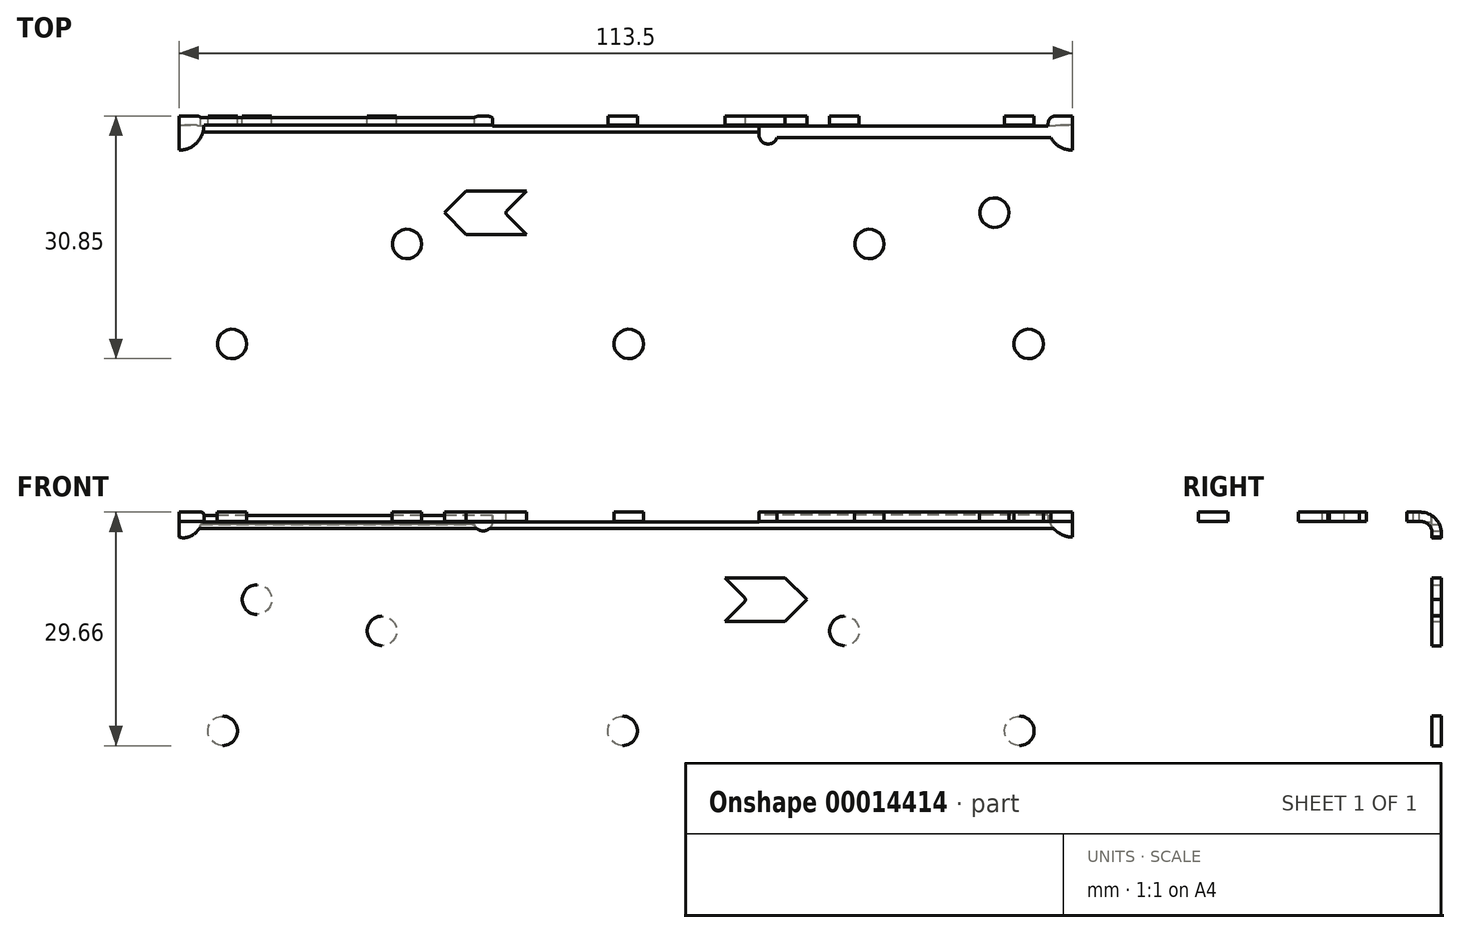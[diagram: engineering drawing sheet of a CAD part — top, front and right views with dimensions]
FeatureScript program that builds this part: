
annotation { "Feature Type Name" : "Feature", "Feature Type Description" : "" }
export const myFeature = defineFeature(function(context is Context, id is Id, definition is map)
    precondition{}
    {
        {
            var Q0;
            Q0=qCreatedBy(makeId("Top.planeOp"),FACE);
            var sketch = newSketch(context, id + "F0", { "sketchPlane" : qUnion([Q0])});
            skLineSegment(sketch, "E0", {"start": v(-34.93, 1.2) * mm, "end": v(-2.51, 1.2) * mm});
            skLineSegment(sketch, "E1", {"start": v(-34.93, 0) * mm, "end": v(-2.64, 0) * mm});
            skLineSegment(sketch, "E2", {"start": v(-1.2, 36.12) * mm, "end": v(-1.2, 2.51) * mm});
            skLineSegment(sketch, "E3", {"start": v(0, 36.12) * mm, "end": v(0, 2.64) * mm});
            skLineSegment(sketch, "E4", {"start": v(-1.2, 36.12) * mm, "end": v(0, 36.12) * mm});
            skLineSegment(sketch, "E5", {"start": v(-34.93, 1.2) * mm, "end": v(-34.93, 0) * mm});
            skLineSegment(sketch, "E6", {"start": v(-14.68, 8.33) * mm, "end": v(-14.68, 1.2) * mm});
            skLineSegment(sketch, "E7", {"start": v(-9.13, 8.33) * mm, "end": v(-9.13, 1.2) * mm});
            skLineSegment(sketch, "E8", {"start": v(-14.68, 8.33) * mm, "end": v(-9.13, 8.33) * mm});
            skArc(sketch, "E9", {"start": v(-2.51, 1.2) * mm, "mid": v(-1.58, 1.58) * mm, "end": v(-1.2, 2.51) * mm});
            skArc(sketch, "E10", {"start": v(-2.64, 0) * mm, "mid": v(-0.77, 0.77) * mm, "end": v(0, 2.64) * mm});
            skSolve(sketch);
        }
        {
            var Q0;
            Q0=makeQuery(id+"F0.imprint","IMPRINT",FACE,{"disambiguationData":[TD([[makeQuery(id+"F0.imprint","IMPRINT",EDGE,{"derivedFrom":sQuery(id+"F0.wireOp",EDGE,"E1")}),1.0]])]});
            extrude(context, id + "F1", {"entities" : qUnion([Q0]), "depth" : 113.5 * mm});
        }
        {
            var Q0;
            Q0=qCreatedBy(makeId("Front.planeOp"),FACE);
            var sketch = newSketch(context, id + "F2", { "sketchPlane" : qUnion([Q0])});
            skLineSegment(sketch, "E11", {"start": v(16.9, 1) * mm, "end": v(16.9, 3.38) * mm});
            skLineSegment(sketch, "E12", {"start": v(19.3, 3.38) * mm, "end": v(19.3, 1) * mm});
            skArc(sketch, "E13", {"start": v(16.9, 1) * mm, "mid": v(18.1, -0.19) * mm, "end": v(19.3, 1) * mm});
            skArc(sketch, "E14", {"start": v(19.3, 3.38) * mm, "mid": v(18.1, 4.57) * mm, "end": v(16.9, 3.38) * mm});
            skLineSegment(sketch, "E15", {"start": v(-47.23, -18.06) * mm, "end": v(-47.23, -18.06) * mm});
            skLineSegment(sketch, "E16", {"start": v(33.73, -5.36) * mm, "end": v(33.73, -5.36) * mm});
            skCircle(sketch, "E17", {"center": v(-50, -10.91) * mm, "radius": 1.88 * mm});
            skCircle(sketch, "E18", {"center": v(0.4, -10.91) * mm, "radius": 1.88 * mm});
            skCircle(sketch, "E19", {"center": v(51.2, -10.91) * mm, "radius": 1.88 * mm});
            skCircle(sketch, "E20", {"center": v(-27.78, 1.79) * mm, "radius": 1.88 * mm});
            skCircle(sketch, "E21", {"center": v(30.96, 1.79) * mm, "radius": 1.88 * mm});
            skCircle(sketch, "E22", {"center": v(46.83, 5.75) * mm, "radius": 1.88 * mm});
            skLineSegment(sketch, "E23", {"start": v(16.9, 15.68) * mm, "end": v(16.9, 16.87) * mm});
            skArc(sketch, "E24", {"start": v(16.9, 15.68) * mm, "mid": v(17.9, 14.5) * mm, "end": v(19.23, 15.28) * mm});
            skLineSegment(sketch, "E25", {"start": v(-56.75, 18.06) * mm, "end": v(-56.75, 16.87) * mm});
            skLineSegment(sketch, "E26", {"start": v(56.75, 16.87) * mm, "end": v(56.75, 18.06) * mm});
            skLineSegment(sketch, "E27", {"start": v(-20.25, 2.98) * mm, "end": v(2.38, 2.98) * mm});
            skLineSegment(sketch, "E28", {"start": v(-20.25, 8.53) * mm, "end": v(2.38, 8.53) * mm});
            skArc(sketch, "E29", {"start": v(-15.08, 6.03) * mm, "mid": v(-15.2, 5.75) * mm, "end": v(-15.08, 5.47) * mm});
            skLineSegment(sketch, "E30", {"start": v(-15.08, 5.47) * mm, "end": v(-12.6, 2.98) * mm});
            skLineSegment(sketch, "E31", {"start": v(-15.08, 6.03) * mm, "end": v(-12.58, 8.53) * mm});
            skLineSegment(sketch, "E32", {"start": v(-23.02, 5.75) * mm, "end": v(-20.25, 2.98) * mm});
            skLineSegment(sketch, "E33", {"start": v(-23.02, 5.75) * mm, "end": v(-20.25, 8.53) * mm});
            skLineSegment(sketch, "E34", {"start": v(-56.75, 16.87) * mm, "end": v(56.75, 16.87) * mm});
            skLineSegment(sketch, "E35", {"start": v(-56.75, 18.06) * mm, "end": v(56.75, 18.06) * mm});
            skArc(sketch, "E36", {"start": v(-56.75, 13.7) * mm, "mid": v(-54.52, 14.63) * mm, "end": v(-53.6, 16.87) * mm});
            skLineSegment(sketch, "E37", {"start": v(-56.75, -18.06) * mm, "end": v(-56.75, 13.7) * mm});
            skLineSegment(sketch, "E38", {"start": v(-56.75, -18.06) * mm, "end": v(-47.23, -18.06) * mm});
            skLineSegment(sketch, "E39", {"start": v(-47.23, -18.06) * mm, "end": v(-34.53, -5.36) * mm});
            skLineSegment(sketch, "E40", {"start": v(-34.53, -5.36) * mm, "end": v(-20.24, -5.36) * mm});
            skLineSegment(sketch, "E41", {"start": v(-20.24, -5.36) * mm, "end": v(-7.54, -18.06) * mm});
            skLineSegment(sketch, "E42", {"start": v(-7.54, -18.06) * mm, "end": v(17.46, -18.06) * mm});
            skLineSegment(sketch, "E43", {"start": v(17.46, -18.06) * mm, "end": v(17.46, -5.36) * mm});
            skLineSegment(sketch, "E44", {"start": v(17.46, -5.36) * mm, "end": v(33.73, -5.36) * mm});
            skLineSegment(sketch, "E45", {"start": v(33.73, -5.36) * mm, "end": v(46.43, -18.06) * mm});
            skLineSegment(sketch, "E46", {"start": v(46.43, -18.06) * mm, "end": v(56.75, -18.06) * mm});
            skLineSegment(sketch, "E47", {"start": v(56.75, -18.06) * mm, "end": v(56.75, 13.7) * mm});
            skLineSegment(sketch, "E48", {"start": v(19.23, 15.28) * mm, "end": v(54, 15.28) * mm});
            skArc(sketch, "E49", {"start": v(54, 15.28) * mm, "mid": v(55.05, 13.92) * mm, "end": v(56.75, 13.7) * mm});
            skLineSegment(sketch, "E50", {"start": v(-47.23, -18.06) * mm, "end": v(-7.54, -18.06) * mm});
            skLineSegment(sketch, "E51", {"start": v(17.46, -18.06) * mm, "end": v(46.43, -18.06) * mm});
            skSolve(sketch);
        }
        {
            var Q0;
            Q0=makeQuery(id+"F1.opExtrude","SWEPT_BODY",BODY,{"disambiguationData":[OSD([sQuery(id+"F0.wireOp",EDGE,"E0"),sQuery(id+"F0.wireOp",EDGE,"E1"),sQuery(id+"F0.wireOp",EDGE,"E2"),sQuery(id+"F0.wireOp",EDGE,"E3"),sQuery(id+"F0.wireOp",EDGE,"E4"),sQuery(id+"F0.wireOp",EDGE,"E5"),sQuery(id+"F0.wireOp",EDGE,"E9"),sQuery(id+"F0.wireOp",EDGE,"E10")])]});
            var Q1;
            Q1=makeQuery(id+"F1.opExtrude","CAP_EDGE",EDGE,{"disambiguationData":[OSD([sQuery(id+"F0.wireOp",EDGE,"E3")])],"isStart":true});
            transform(context, id + "F3", {"entities" : qUnion([Q0]), "transformType" : TransformType.ROTATION, "transformAxis" : qUnion([Q1]), "angle" : 90 * degree, "makeCopy" : false});
        }
        {
            var Q0;
            Q0=makeQuery(id+"F1.opExtrude","SWEPT_BODY",BODY,{"disambiguationData":[OSD([sQuery(id+"F0.wireOp",EDGE,"E0"),sQuery(id+"F0.wireOp",EDGE,"E1"),sQuery(id+"F0.wireOp",EDGE,"E2"),sQuery(id+"F0.wireOp",EDGE,"E3"),sQuery(id+"F0.wireOp",EDGE,"E4"),sQuery(id+"F0.wireOp",EDGE,"E5"),sQuery(id+"F0.wireOp",EDGE,"E9"),sQuery(id+"F0.wireOp",EDGE,"E10")])]});
            var Q1;
            Q1=makeQuery(id+"F1.opExtrude","CAP_VERTEX",VERTEX,{"disambiguationData":[OSD([sQuery(id+"F0.wireOp",EDGE,"E1"),sQuery(id+"F0.wireOp",EDGE,"E5")])],"isStart":false});
            var Q2;
            Q2=sQuery(id+"F2.wireOp",VERTEX,"E38.start");
            transform(context, id + "F4", {"entities" : qUnion([Q0]), "transformType" : TransformType.TRANSLATION_ENTITY, "oppositeDirectionEntity" : false, "transformLine" : qUnion([Q1, Q2]), "makeCopy" : false});
        }
        {
            var Q0;
            Q0=makeQuery(id+"F2.imprint","IMPRINT",FACE,{"disambiguationData":[TD([[makeQuery(id+"F2.imprint","IMPRINT",EDGE,{"derivedFrom":sQuery(id+"F2.wireOp",EDGE,"E39")}),-1.0]])]});
            var Q1;
            Q1=makeQuery(id+"F2.imprint","IMPRINT",FACE,{"disambiguationData":[TD([[makeQuery(id+"F2.imprint","IMPRINT",EDGE,{"derivedFrom":sQuery(id+"F2.wireOp",EDGE,"E43")}),-1.0]])]});
            var Q2;
            Q2=makeQuery(id+"F2.imprint","IMPRINT",FACE,{"disambiguationData":[TD([[makeQuery(id+"F2.imprint","IMPRINT",EDGE,{"derivedFrom":sQuery(id+"F2.wireOp",EDGE,"E17")}),-1.0]])]});
            var Q3;
            Q3=makeQuery(id+"F2.imprint","IMPRINT",FACE,{"disambiguationData":[TD([[makeQuery(id+"F2.imprint","IMPRINT",EDGE,{"derivedFrom":sQuery(id+"F2.wireOp",EDGE,"E21")}),-1.0]])]});
            var Q4;
            Q4=makeQuery(id+"F2.imprint","IMPRINT",FACE,{"disambiguationData":[TD([[makeQuery(id+"F2.imprint","IMPRINT",EDGE,{"derivedFrom":sQuery(id+"F2.wireOp",EDGE,"E22")}),-1.0]])]});
            var Q5;
            Q5=makeQuery(id+"F2.imprint","IMPRINT",FACE,{"disambiguationData":[TD([[makeQuery(id+"F2.imprint","IMPRINT",EDGE,{"derivedFrom":sQuery(id+"F2.wireOp",EDGE,"E19")}),-1.0]])]});
            var Q6;
            Q6=makeQuery(id+"F2.imprint","IMPRINT",FACE,{"disambiguationData":[TD([[makeQuery(id+"F2.imprint","IMPRINT",EDGE,{"derivedFrom":sQuery(id+"F2.wireOp",EDGE,"E18")}),-1.0]])]});
            var Q7;
            Q7=makeQuery(id+"F2.imprint","IMPRINT",FACE,{"disambiguationData":[TD([[makeQuery(id+"F2.imprint","IMPRINT",EDGE,{"derivedFrom":sQuery(id+"F2.wireOp",EDGE,"E20")}),-1.0]])]});
            var Q8;
            Q8=makeQuery(id+"F2.imprint","IMPRINT",FACE,{"disambiguationData":[TD([[makeQuery(id+"F2.imprint","IMPRINT",EDGE,{"derivedFrom":sQuery(id+"F2.wireOp",EDGE,"E11")}),-1.0]])]});
            extrude(context, id + "F5", {"entities" : qUnion([Q0, Q1, Q2, Q3, Q4, Q5, Q6, Q7, Q8]), "operationType" : NewBodyOperationType.REMOVE, "oppositeDirection" : true, "depth" : 1.27 * mm});
        }
        {
            var Q0;
            Q0=makeQuery(id+"F1.opExtrude","SWEPT_BODY",BODY,{"disambiguationData":[OSD([sQuery(id+"F0.wireOp",EDGE,"E0"),sQuery(id+"F0.wireOp",EDGE,"E1"),sQuery(id+"F0.wireOp",EDGE,"E2"),sQuery(id+"F0.wireOp",EDGE,"E3"),sQuery(id+"F0.wireOp",EDGE,"E4"),sQuery(id+"F0.wireOp",EDGE,"E5"),sQuery(id+"F0.wireOp",EDGE,"E9"),sQuery(id+"F0.wireOp",EDGE,"E10")])]});
            var Q1;
            Q1=makeQuery(id+"F1.opExtrude","CAP_EDGE",EDGE,{"disambiguationData":[OSD([sQuery(id+"F0.wireOp",EDGE,"E1")])],"isStart":false});
            transform(context, id + "F6", {"entities" : qUnion([Q0]), "transformType" : TransformType.TRANSLATION_DISTANCE, "transformDirection" : qUnion([Q1]), "distance" : 17.07 * mm, "oppositeDirection" : true, "makeCopy" : false});
        }
        {
            var Q0;
            Q0=qCreatedBy(makeId("Top.planeOp"),FACE);
            var sketch = newSketch(context, id + "F7", { "sketchPlane" : qUnion([Q0])});
            skLineSegment(sketch, "E52", {"start": v(16.9, 1) * mm, "end": v(16.9, 3.38) * mm});
            skLineSegment(sketch, "E53", {"start": v(19.3, 3.38) * mm, "end": v(19.3, 1) * mm});
            skArc(sketch, "E54", {"start": v(16.9, 1) * mm, "mid": v(18.1, -0.19) * mm, "end": v(19.3, 1) * mm});
            skArc(sketch, "E55", {"start": v(19.3, 3.38) * mm, "mid": v(18.1, 4.57) * mm, "end": v(16.9, 3.38) * mm});
            skLineSegment(sketch, "E56", {"start": v(33.73, -5.36) * mm, "end": v(33.73, -5.36) * mm});
            skCircle(sketch, "E57", {"center": v(-50, -10.91) * mm, "radius": 1.88 * mm});
            skCircle(sketch, "E58", {"center": v(0.4, -10.91) * mm, "radius": 1.88 * mm});
            skCircle(sketch, "E59", {"center": v(51.2, -10.91) * mm, "radius": 1.88 * mm});
            skCircle(sketch, "E60", {"center": v(-27.78, 1.79) * mm, "radius": 1.88 * mm});
            skCircle(sketch, "E61", {"center": v(30.96, 1.79) * mm, "radius": 1.88 * mm});
            skCircle(sketch, "E62", {"center": v(46.83, 5.75) * mm, "radius": 1.88 * mm});
            skArc(sketch, "E63", {"start": v(16.9, 15.68) * mm, "mid": v(17.9, 14.5) * mm, "end": v(19.23, 15.28) * mm});
            skLineSegment(sketch, "E64", {"start": v(-20.25, 2.98) * mm, "end": v(2.38, 2.98) * mm});
            skLineSegment(sketch, "E65", {"start": v(-20.25, 8.53) * mm, "end": v(2.38, 8.53) * mm});
            skArc(sketch, "E66", {"start": v(-15.08, 6.03) * mm, "mid": v(-15.2, 5.75) * mm, "end": v(-15.08, 5.47) * mm});
            skLineSegment(sketch, "E67", {"start": v(-15.08, 5.47) * mm, "end": v(-12.6, 2.98) * mm});
            skLineSegment(sketch, "E68", {"start": v(-15.08, 6.03) * mm, "end": v(-12.58, 8.53) * mm});
            skLineSegment(sketch, "E69", {"start": v(-23.02, 5.75) * mm, "end": v(-20.25, 2.98) * mm});
            skLineSegment(sketch, "E70", {"start": v(-23.02, 5.75) * mm, "end": v(-20.25, 8.53) * mm});
            skLineSegment(sketch, "E71", {"start": v(-56.75, 18.06) * mm, "end": v(56.75, 18.06) * mm});
            skLineSegment(sketch, "E72", {"start": v(-56.75, 16.87) * mm, "end": v(56.75, 16.87) * mm});
            skLineSegment(sketch, "E73", {"start": v(-56.75, 18.06) * mm, "end": v(-56.75, 16.87) * mm});
            skLineSegment(sketch, "E74", {"start": v(56.75, 18.06) * mm, "end": v(56.75, 16.87) * mm});
            skLineSegment(sketch, "E75", {"start": v(-56.75, 13.7) * mm, "end": v(-56.75, -18.06) * mm});
            skLineSegment(sketch, "E76", {"start": v(56.75, 13.7) * mm, "end": v(56.75, -18.06) * mm});
            skLineSegment(sketch, "E77", {"start": v(-7.54, -18.06) * mm, "end": v(17.46, -18.06) * mm});
            skLineSegment(sketch, "E78", {"start": v(17.46, -18.06) * mm, "end": v(46.43, -18.06) * mm});
            skLineSegment(sketch, "E79", {"start": v(46.43, -18.06) * mm, "end": v(56.75, -18.06) * mm});
            skArc(sketch, "E80", {"start": v(-56.75, 13.7) * mm, "mid": v(-54.5, 14.62) * mm, "end": v(-53.58, 16.87) * mm});
            skArc(sketch, "E81", {"start": v(54, 15.28) * mm, "mid": v(55.17, 14.12) * mm, "end": v(56.75, 13.7) * mm});
            skLineSegment(sketch, "E82", {"start": v(19.23, 15.28) * mm, "end": v(54, 15.28) * mm});
            skLineSegment(sketch, "E83", {"start": v(16.9, 15.68) * mm, "end": v(16.9, 16.87) * mm});
            skLineSegment(sketch, "E84", {"start": v(-34.53, -5.36) * mm, "end": v(-20.24, -5.36) * mm});
            skLineSegment(sketch, "E85", {"start": v(-7.54, -18.06) * mm, "end": v(-20.24, -5.36) * mm});
            skLineSegment(sketch, "E86", {"start": v(17.46, -5.36) * mm, "end": v(33.73, -5.36) * mm});
            skLineSegment(sketch, "E87", {"start": v(17.46, -5.36) * mm, "end": v(17.46, -18.06) * mm});
            skLineSegment(sketch, "E88", {"start": v(46.43, -18.06) * mm, "end": v(33.73, -5.36) * mm});
            skLineSegment(sketch, "E89", {"start": v(-34.53, -5.36) * mm, "end": v(-47.23, -18.06) * mm});
            skLineSegment(sketch, "E90", {"start": v(-56.75, -18.06) * mm, "end": v(-47.23, -18.06) * mm});
            skLineSegment(sketch, "E91", {"start": v(-47.23, -18.06) * mm, "end": v(-7.54, -18.06) * mm});
            skSolve(sketch);
        }
        {
            var Q0;
            Q0=makeQuery(id+"F1.opExtrude","SWEPT_BODY",BODY,{"disambiguationData":[OSD([sQuery(id+"F0.wireOp",EDGE,"E0"),sQuery(id+"F0.wireOp",EDGE,"E1"),sQuery(id+"F0.wireOp",EDGE,"E2"),sQuery(id+"F0.wireOp",EDGE,"E3"),sQuery(id+"F0.wireOp",EDGE,"E4"),sQuery(id+"F0.wireOp",EDGE,"E5"),sQuery(id+"F0.wireOp",EDGE,"E9"),sQuery(id+"F0.wireOp",EDGE,"E10")])]});
            var Q1;
            Q1=makeQuery(id+"F1.opExtrude","CAP_EDGE",EDGE,{"disambiguationData":[OSD([sQuery(id+"F0.wireOp",EDGE,"E1")])],"isStart":false});
            transform(context, id + "F8", {"entities" : qUnion([Q0]), "transformType" : TransformType.ROTATION, "transformAxis" : qUnion([Q1]), "angle" : 180 * degree, "makeCopy" : false});
        }
        {
            var Q0;
            Q0=makeQuery(id+"F1.opExtrude","SWEPT_BODY",BODY,{"disambiguationData":[OSD([sQuery(id+"F0.wireOp",EDGE,"E0"),sQuery(id+"F0.wireOp",EDGE,"E1"),sQuery(id+"F0.wireOp",EDGE,"E2"),sQuery(id+"F0.wireOp",EDGE,"E3"),sQuery(id+"F0.wireOp",EDGE,"E4"),sQuery(id+"F0.wireOp",EDGE,"E5"),sQuery(id+"F0.wireOp",EDGE,"E9"),sQuery(id+"F0.wireOp",EDGE,"E10")])]});
            var Q1;
            Q1=makeQuery(id+"F1.opExtrude","CAP_VERTEX",VERTEX,{"disambiguationData":[OSD([sQuery(id+"F0.wireOp",EDGE,"E3"),sQuery(id+"F0.wireOp",EDGE,"E4")])],"isStart":false});
            var Q2;
            Q2=sQuery(id+"F7.wireOp",VERTEX,"E76.end");
            transform(context, id + "F9", {"entities" : qUnion([Q0]), "transformType" : TransformType.TRANSLATION_ENTITY, "oppositeDirectionEntity" : false, "transformLine" : qUnion([Q1, Q2]), "makeCopy" : false});
        }
        {
            var Q0;
            Q0=makeQuery(id+"F7.imprint","IMPRINT",FACE,{"disambiguationData":[TD([[makeQuery(id+"F7.imprint","IMPRINT",EDGE,{"derivedFrom":sQuery(id+"F7.wireOp",EDGE,"E57")}),-1.0]])]});
            var Q1;
            Q1=makeQuery(id+"F7.imprint","IMPRINT",FACE,{"disambiguationData":[TD([[makeQuery(id+"F7.imprint","IMPRINT",EDGE,{"derivedFrom":sQuery(id+"F7.wireOp",EDGE,"E59")}),-1.0]])]});
            var Q2;
            Q2=makeQuery(id+"F7.imprint","IMPRINT",FACE,{"disambiguationData":[TD([[makeQuery(id+"F7.imprint","IMPRINT",EDGE,{"derivedFrom":sQuery(id+"F7.wireOp",EDGE,"E58")}),-1.0]])]});
            var Q3;
            Q3=makeQuery(id+"F7.imprint","IMPRINT",FACE,{"disambiguationData":[TD([[makeQuery(id+"F7.imprint","IMPRINT",EDGE,{"derivedFrom":sQuery(id+"F7.wireOp",EDGE,"E62")}),-1.0]])]});
            var Q4;
            Q4=makeQuery(id+"F7.imprint","IMPRINT",FACE,{"disambiguationData":[TD([[makeQuery(id+"F7.imprint","IMPRINT",EDGE,{"derivedFrom":sQuery(id+"F7.wireOp",EDGE,"E78")}),1.0]])]});
            var Q5;
            Q5=makeQuery(id+"F7.imprint","IMPRINT",FACE,{"disambiguationData":[TD([[makeQuery(id+"F7.imprint","IMPRINT",EDGE,{"derivedFrom":sQuery(id+"F7.wireOp",EDGE,"E61")}),-1.0]])]});
            var Q6;
            Q6=makeQuery(id+"F7.imprint","IMPRINT",FACE,{"disambiguationData":[TD([[makeQuery(id+"F7.imprint","IMPRINT",EDGE,{"derivedFrom":sQuery(id+"F7.wireOp",EDGE,"E60")}),-1.0]])]});
            var Q7;
            Q7=makeQuery(id+"F7.imprint","IMPRINT",FACE,{"disambiguationData":[TD([[makeQuery(id+"F7.imprint","IMPRINT",EDGE,{"derivedFrom":sQuery(id+"F7.wireOp",EDGE,"E52")}),-1.0]])]});
            var Q8;
            Q8=makeQuery(id+"F7.imprint","IMPRINT",FACE,{"disambiguationData":[TD([[makeQuery(id+"F7.imprint","IMPRINT",EDGE,{"derivedFrom":sQuery(id+"F7.wireOp",EDGE,"E84")}),-1.0]])]});
            extrude(context, id + "F10", {"entities" : qUnion([Q0, Q1, Q2, Q3, Q4, Q5, Q6, Q7, Q8]), "operationType" : NewBodyOperationType.REMOVE, "oppositeDirection" : true, "depth" : 1.27 * mm});
        }
    });
